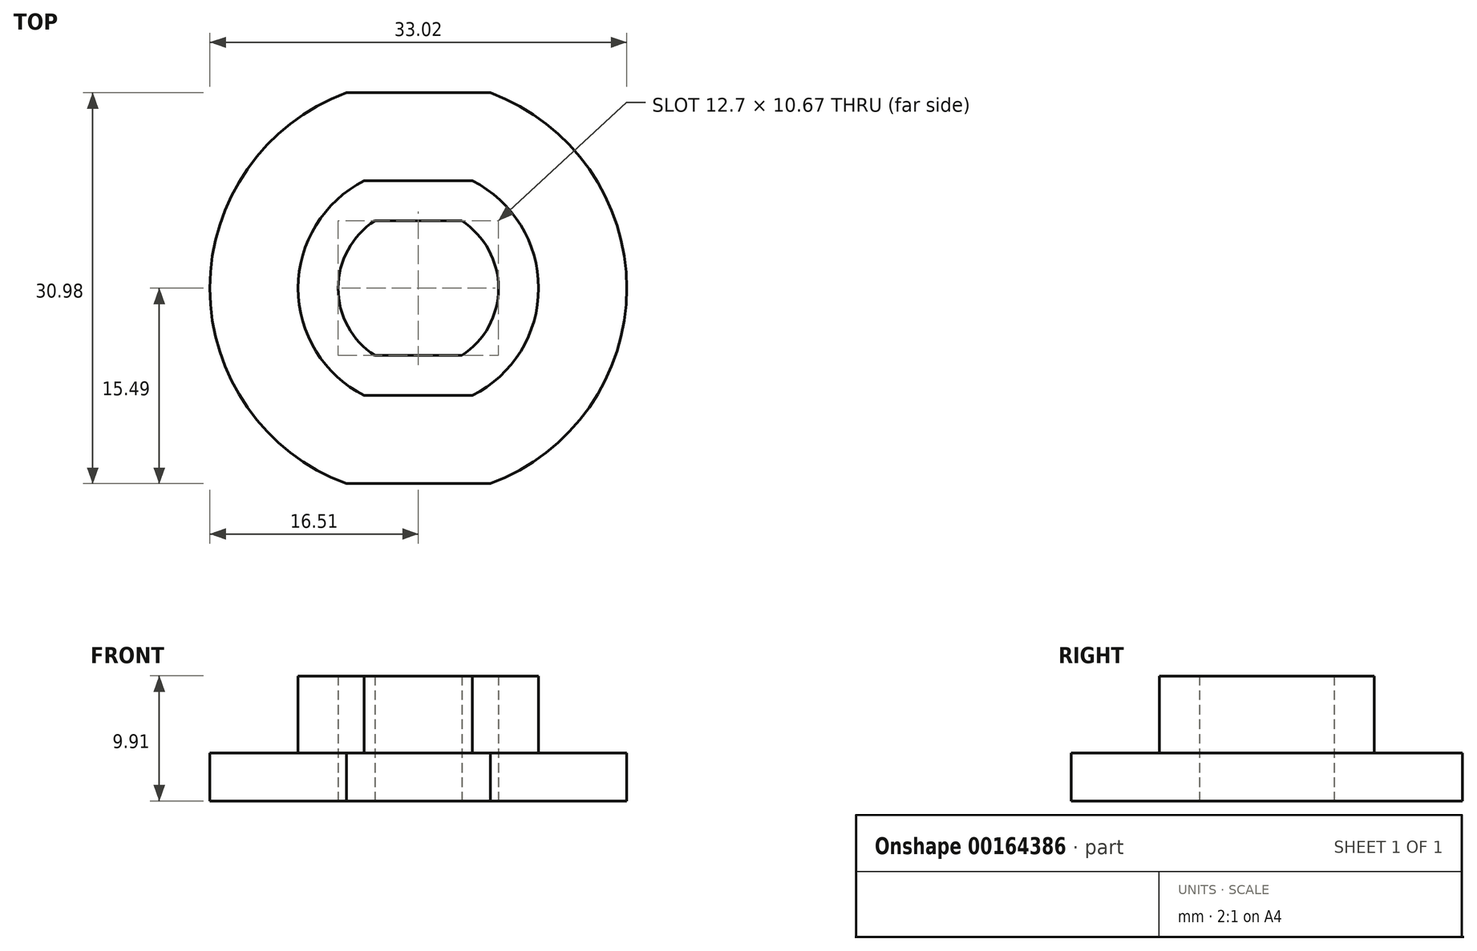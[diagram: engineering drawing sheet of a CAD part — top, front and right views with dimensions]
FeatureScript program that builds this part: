
annotation { "Feature Type Name" : "Feature", "Feature Type Description" : "" }
export const myFeature = defineFeature(function(context is Context, id is Id, definition is map)
    precondition{}
    {
        {
            var Q0;
            Q0=qCreatedBy(makeId("Top.planeOp"),FACE);
            var sketch = newSketch(context, id + "F0", { "sketchPlane" : qUnion([Q0])});
            skArc(sketch, "E0", {"start": v(-3.45, 5.33) * mm, "mid": v(-6.35, 0) * mm, "end": v(-3.45, -5.33) * mm});
            skLineSegment(sketch, "E1", {"start": v(-3.45, 5.33) * mm, "end": v(3.45, 5.33) * mm});
            skLineSegment(sketch, "E2", {"start": v(3.45, -5.33) * mm, "end": v(-3.45, -5.33) * mm});
            skArc(sketch, "E3.trimOffspring", {"start": v(3.45, -5.33) * mm, "mid": v(6.35, 0) * mm, "end": v(3.45, 5.33) * mm});
            skLineSegment(sketch, "E4", {"start": v(-12.64, 0) * mm, "end": v(12.64, 0) * mm});
            skArc(sketch, "E5.0", {"start": v(4.28, -8.5) * mm, "mid": v(9.52, 0) * mm, "end": v(4.28, 8.5) * mm});
            skLineSegment(sketch, "E5.1", {"start": v(4.28, -8.5) * mm, "end": v(-4.28, -8.5) * mm});
            skArc(sketch, "E5.2", {"start": v(-4.28, 8.5) * mm, "mid": v(-9.52, 0) * mm, "end": v(-4.28, -8.5) * mm});
            skLineSegment(sketch, "E5.3", {"start": v(-4.28, 8.5) * mm, "end": v(4.28, 8.5) * mm});
            skArc(sketch, "E6.0", {"start": v(-5.7, 15.5) * mm, "mid": v(-16.51, 0) * mm, "end": v(-5.7, -15.5) * mm});
            skLineSegment(sketch, "E6.1", {"start": v(-5.7, 15.5) * mm, "end": v(5.7, 15.5) * mm});
            skArc(sketch, "E6.2", {"start": v(5.7, -15.5) * mm, "mid": v(16.51, 0) * mm, "end": v(5.7, 15.5) * mm});
            skLineSegment(sketch, "E6.3", {"start": v(5.7, -15.5) * mm, "end": v(-5.7, -15.5) * mm});
            skSolve(sketch);
        }
        {
            var Q0;
            {var subQ4=sQuery(id+"F0.wireOp",EDGE,"E5.1");Q0=makeQuery(id+"F0.imprint","IMPRINT",FACE,{"disambiguationData":[TD([[makeQuery(id+"F0.imprint","IMPRINT",EDGE,{"derivedFrom":subQ4}),1.0]])]});}
            extrude(context, id + "F1", {"entities" : qUnion([Q0]), "depth" : 3.8 * mm});
        }
        {
            var Q0;
            {var subQ7=sQuery(id+"F0.wireOp",EDGE,"E2");Q0=makeQuery(id+"F0.imprint","IMPRINT",FACE,{"disambiguationData":[TD([[makeQuery(id+"F0.imprint","IMPRINT",EDGE,{"derivedFrom":subQ7}),1.0]])]});}
            var Q1;
            {var subQ6=sQuery(id+"F0.wireOp",EDGE,"E1");Q1=makeQuery(id+"F0.imprint","IMPRINT",FACE,{"disambiguationData":[TD([[makeQuery(id+"F0.imprint","IMPRINT",EDGE,{"derivedFrom":subQ6}),1.0]])]});}
            extrude(context, id + "F2", {"entities" : qUnion([Q0, Q1]), "operationType" : NewBodyOperationType.ADD, "depth" : 9.9 * mm});
        }
    });
